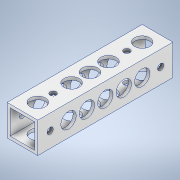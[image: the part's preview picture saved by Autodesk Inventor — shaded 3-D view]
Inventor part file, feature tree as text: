
AUTODESK INVENTOR PART (.ipt)
format: ipt  version: 2020.3 (Build 243373000, 373)  size: 208,896 bytes
history: native  units: mm
features: sketch x5, hole x4, other x1, extrude x1
ambient origin geometry x8: Origin, YZ Plane, XZ Plane, XY Plane, X Axis, Y Axis, Z Axis, Center Point
bodies: Body1 (feature_tree)
feature tree (11):
  other  "ソリッド1"
  extrude  "押し出し1"  Depth=15.0mm
  hole  "穴1"  [1 undecoded]
  hole  "穴2"  [1 undecoded]
  hole  "穴3"  [1 undecoded]
  hole  "穴4"  [1 undecoded]
  sketch  "スケッチ1"
  sketch  "スケッチ2"
  sketch  "スケッチ3"
  sketch  "スケッチ4"
  sketch  "スケッチ5"
note: 4 required parameter values undecoded (feature->parameter linkage not recoverable at this tier; creation-order binding heuristic only, values carry confidence <= 0.55)
